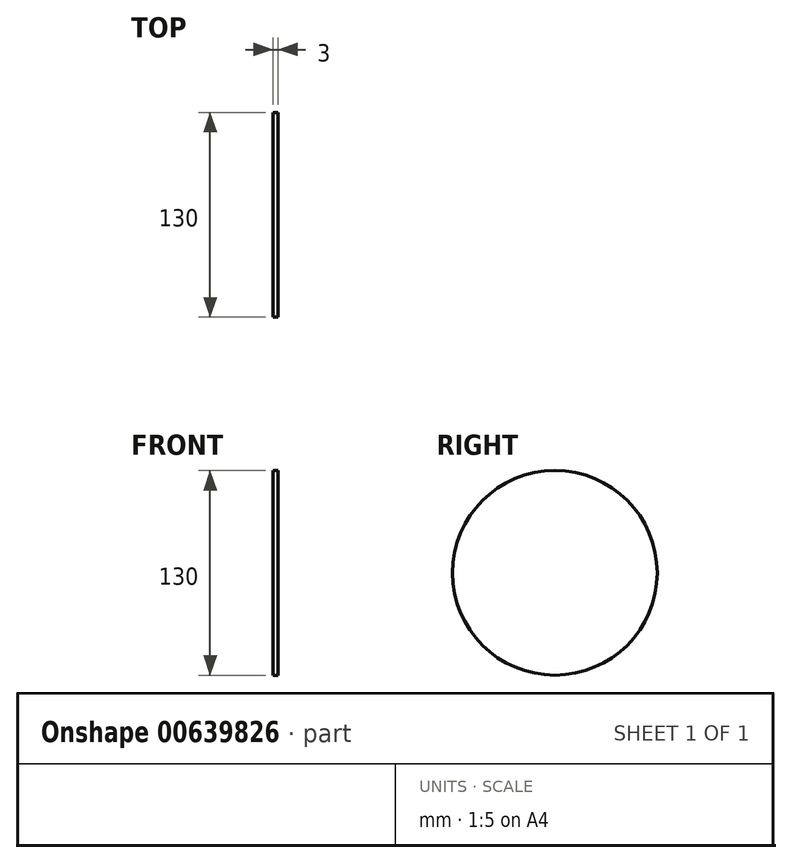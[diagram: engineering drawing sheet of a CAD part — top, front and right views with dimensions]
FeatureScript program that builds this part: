
annotation { "Feature Type Name" : "Feature", "Feature Type Description" : "" }
export const myFeature = defineFeature(function(context is Context, id is Id, definition is map)
    precondition{}
    {
        {
            var Q0;
            Q0=qCreatedBy(makeId("Right.planeOp"),FACE);
            var sketch = newSketch(context, id + "F0", { "sketchPlane" : qUnion([Q0])});
            skCircle(sketch, "E0", {"center": v(0, 0) * mm, "radius": 65 * mm});
            skSolve(sketch);
        }
        {
            var Q0;
            Q0 = qSketchRegion(id + "F0", true);
            extrude(context, id + "F1", {"entities" : qUnion([Q0]), "depth" : 3 * mm, "offsetDistance" : 25 * mm});
        }
    });
